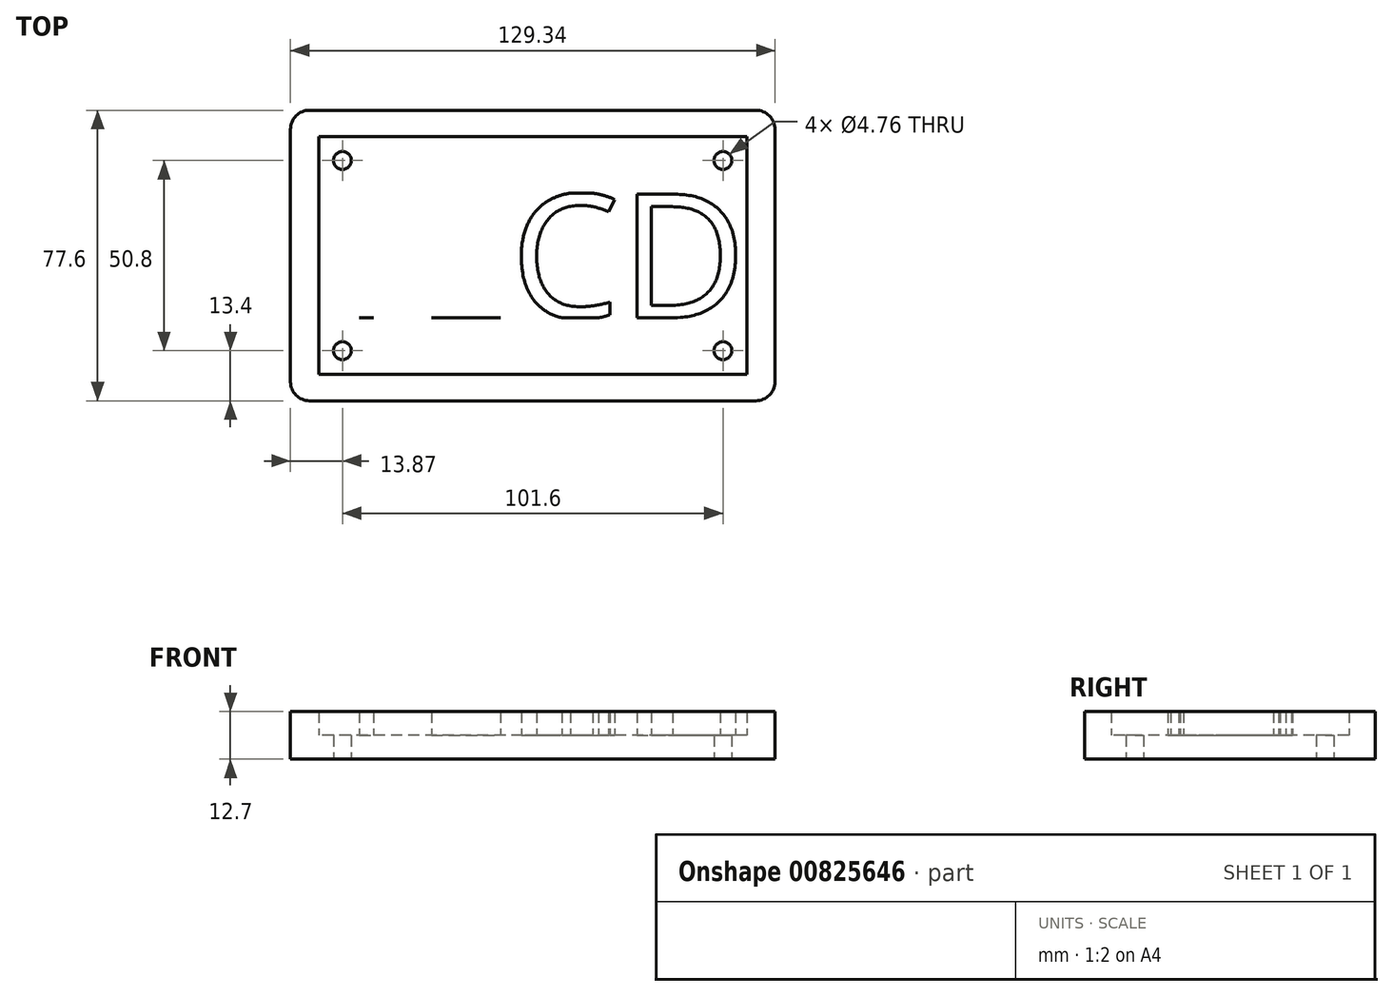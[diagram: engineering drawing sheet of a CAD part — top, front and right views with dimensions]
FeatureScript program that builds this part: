
annotation { "Feature Type Name" : "Feature", "Feature Type Description" : "" }
export const myFeature = defineFeature(function(context is Context, id is Id, definition is map)
    precondition{}
    {
        {
            var Q0;
            Q0=qCreatedBy(makeId("Top.planeOp"),FACE);
            var sketch = newSketch(context, id + "F0", { "sketchPlane" : qUnion([Q0])});
            skLineSegment(sketch, "E0.bottom", {"start": v(63.5, -38.1) * mm, "end": v(-63.5, -38.1) * mm});
            skLineSegment(sketch, "E0.top", {"start": v(63.5, 38.1) * mm, "end": v(-63.5, 38.1) * mm});
            skLineSegment(sketch, "E0.left", {"start": v(63.5, -38.1) * mm, "end": v(63.5, 38.1) * mm});
            skLineSegment(sketch, "E0.right", {"start": v(-63.5, -38.1) * mm, "end": v(-63.5, 38.1) * mm});
            skPoint(sketch, "E0.middle", {"position": v(0, 0) * mm});
            skSolve(sketch);
        }
        {
            var Q0;
            Q0=makeQuery(id+"F0.imprint","IMPRINT",FACE,{"disambiguationData":[TD([[makeQuery(id+"F0.imprint","IMPRINT",EDGE,{"derivedFrom":sQuery(id+"F0.wireOp",EDGE,"E0.bottom")}),-1.0]])]});
            extrude(context, id + "F1", {"entities" : qUnion([Q0]), "depth" : 6.35 * mm, "offsetDistance" : 25.4 * mm});
        }
        {
            var Q0;
            Q0=makeQuery(id+"F1.opExtrude","SWEPT_EDGE",EDGE,{"disambiguationData":[OSD([sQuery(id+"F0.wireOp",EDGE,"E0.top"),sQuery(id+"F0.wireOp",EDGE,"E0.right")])]});
            var Q1;
            Q1=makeQuery(id+"F1.opExtrude","SWEPT_EDGE",EDGE,{"disambiguationData":[OSD([sQuery(id+"F0.wireOp",EDGE,"E0.bottom"),sQuery(id+"F0.wireOp",EDGE,"E0.right")])]});
            var Q2;
            Q2=makeQuery(id+"F1.opExtrude","SWEPT_EDGE",EDGE,{"disambiguationData":[OSD([sQuery(id+"F0.wireOp",EDGE,"E0.bottom"),sQuery(id+"F0.wireOp",EDGE,"E0.left")])]});
            var Q3;
            Q3=makeQuery(id+"F1.opExtrude","SWEPT_EDGE",EDGE,{"disambiguationData":[OSD([sQuery(id+"F0.wireOp",EDGE,"E0.top"),sQuery(id+"F0.wireOp",EDGE,"E0.left")])]});
            fillet(context, id + "F2", {"entities" : qUnion([Q0, Q1, Q2, Q3]), "radius" : 5.08 * mm, "tangentPropagation" : true, "allowEdgeOverflow" : false});
        }
        {
            var Q0;
            Q0=makeQuery(id+"F1.opExtrude","CAP_FACE",FACE,{"disambiguationData":[OSD([sQuery(id+"F0.wireOp",EDGE,"E0.bottom"),sQuery(id+"F0.wireOp",EDGE,"E0.top"),sQuery(id+"F0.wireOp",EDGE,"E0.left"),sQuery(id+"F0.wireOp",EDGE,"E0.right")])],"isStart":false});
            cPlane(context, id + "F3", {"entities" : qUnion([Q0]), "cplaneType" : CPlaneType.OFFSET, "offset" : 0 * mm, "width" : 152.4 * mm, "height" : 152.4 * mm});
        }
        {
            var Q0;
            Q0=qCreatedBy(id+"F3.planeOp",FACE);
            var sketch = newSketch(context, id + "F4", { "sketchPlane" : qUnion([Q0])});
            skLineSegment(sketch, "E1.bottom", {"start": v(-64.67, 38.8) * mm, "end": v(64.67, 38.8) * mm});
            skLineSegment(sketch, "E1.top", {"start": v(-64.67, -38.8) * mm, "end": v(64.67, -38.8) * mm});
            skLineSegment(sketch, "E1.left", {"start": v(-64.67, 38.8) * mm, "end": v(-64.67, -38.8) * mm});
            skLineSegment(sketch, "E1.right", {"start": v(64.67, 38.8) * mm, "end": v(64.67, -38.8) * mm});
            skPoint(sketch, "E1.middle", {"position": v(0, 0) * mm});
            skLineSegment(sketch, "E2.bottom", {"start": v(-57.15, 16.64) * mm, "end": v(57.15, 16.64) * mm});
            skLineSegment(sketch, "E2.top", {"start": v(-57.15, -16.64) * mm, "end": v(57.15, -16.64) * mm});
            skLineSegment(sketch, "E2.left", {"start": v(-57.15, 16.64) * mm, "end": v(-57.15, -16.64) * mm});
            skLineSegment(sketch, "E2.right", {"start": v(57.15, 16.64) * mm, "end": v(57.15, -16.64) * mm});
            skPoint(sketch, "E3", {"position": v(-57.15, 16.64) * mm});
            skPoint(sketch, "E4", {"position": v(57.15, -16.64) * mm});
            skText(sketch, "E5", { "text": "TECD", "fontName": "OpenSans-Regular.ttf"});
            skLineSegment(sketch, "E6.bottom", {"start": v(57.15, -31.75) * mm, "end": v(-57.15, -31.75) * mm});
            skLineSegment(sketch, "E6.top", {"start": v(57.15, 31.75) * mm, "end": v(-57.15, 31.75) * mm});
            skLineSegment(sketch, "E6.left", {"start": v(57.15, -31.75) * mm, "end": v(57.15, 31.75) * mm});
            skLineSegment(sketch, "E6.right", {"start": v(-57.15, -31.75) * mm, "end": v(-57.15, 31.75) * mm});
            const initialGuessF4  = {"E5": [-0.05715, -0.01664, 1, 0, 0.03328]};
            skSetInitialGuess(sketch, initialGuessF4);
            skSolve(sketch);
        }
        {
            var Q0;
            Q0=makeQuery(id+"F4.imprint","IMPRINT",FACE,{"disambiguationData":[TD([[makeQuery(id+"F4.imprint","IMPRINT",EDGE,{"derivedFrom":sQuery(id+"F4.wireOp",EDGE,"E1.bottom")}),-1.0]])]});
            extrude(context, id + "F5", {"entities" : qUnion([Q0]), "operationType" : NewBodyOperationType.ADD, "depth" : 6.35 * mm, "offsetDistance" : 25.4 * mm});
        }
        {
            var Q0;
            Q0=makeQuery(id+"F5.opExtrude","SWEPT_EDGE",EDGE,{"disambiguationData":[OSD([sQuery(id+"F4.wireOp",EDGE,"E1.top"),sQuery(id+"F4.wireOp",EDGE,"E1.left")])]});
            var Q1;
            Q1=makeQuery(id+"F5.opExtrude","SWEPT_EDGE",EDGE,{"disambiguationData":[OSD([sQuery(id+"F4.wireOp",EDGE,"E1.bottom"),sQuery(id+"F4.wireOp",EDGE,"E1.right")])]});
            var Q2;
            Q2=makeQuery(id+"F5.opExtrude","SWEPT_EDGE",EDGE,{"disambiguationData":[OSD([sQuery(id+"F4.wireOp",EDGE,"E1.top"),sQuery(id+"F4.wireOp",EDGE,"E1.right")])]});
            var Q3;
            Q3=makeQuery(id+"F5.opExtrude","SWEPT_EDGE",EDGE,{"disambiguationData":[OSD([sQuery(id+"F4.wireOp",EDGE,"E1.bottom"),sQuery(id+"F4.wireOp",EDGE,"E1.left")])]});
            fillet(context, id + "F6", {"entities" : qUnion([Q0, Q1, Q2, Q3]), "radius" : 5.08 * mm, "tangentPropagation" : true, "allowEdgeOverflow" : false});
        }
        {
            var Q0;
            {var subQ0=sQuery(id+"F4.wireOp",EDGE,"E5.sketch_text.stroke-1");Q0=makeQuery(id+"F4.imprint","IMPRINT",FACE,{"disambiguationData":[TD([[makeQuery(id+"F4.imprint","IMPRINT",EDGE,{"derivedFrom":subQ0}),-1.0]])]});}
            var Q1;
            {var subQ0=sQuery(id+"F4.wireOp",EDGE,"E5.sketch_text.stroke-9");Q1=makeQuery(id+"F4.imprint","IMPRINT",FACE,{"disambiguationData":[TD([[makeQuery(id+"F4.imprint","IMPRINT",EDGE,{"derivedFrom":subQ0}),-1.0]])]});}
            var Q2;
            Q2=makeQuery(id+"F4.imprint","IMPRINT",FACE,{"disambiguationData":[TD([[makeQuery(id+"F4.imprint","IMPRINT",EDGE,{"derivedFrom":sQuery(id+"F4.wireOp",EDGE,"E5.sketch_text.stroke-20")}),-1.0]])]});
            var Q3;
            Q3=makeQuery(id+"F4.imprint","IMPRINT",FACE,{"disambiguationData":[TD([[makeQuery(id+"F4.imprint","IMPRINT",EDGE,{"derivedFrom":sQuery(id+"F4.wireOp",EDGE,"E5.sketch_text.stroke-35")}),-1.0]])]});
            extrude(context, id + "F7", {"entities" : qUnion([Q0, Q1, Q2, Q3]), "operationType" : NewBodyOperationType.ADD, "depth" : 6.35 * mm, "offsetDistance" : 25.4 * mm});
        }
        {
            var Q0;
            Q0=makeQuery(id+"F1.opExtrude","CAP_FACE",FACE,{"disambiguationData":[OSD([sQuery(id+"F0.wireOp",EDGE,"E0.bottom"),sQuery(id+"F0.wireOp",EDGE,"E0.top"),sQuery(id+"F0.wireOp",EDGE,"E0.left"),sQuery(id+"F0.wireOp",EDGE,"E0.right")])],"isStart":true});
            var sketch = newSketch(context, id + "F8", { "sketchPlane" : qUnion([Q0])});
            skCircle(sketch, "E7.1.1.0", {"center": v(-50.8, 25.4) * mm, "radius": 2.38 * mm});
            skCircle(sketch, "E8.1.1.0", {"center": v(50.8, 25.4) * mm, "radius": 2.38 * mm});
            skCircle(sketch, "E9.1.1.0", {"center": v(50.8, -25.4) * mm, "radius": 2.38 * mm});
            skCircle(sketch, "E10.1.1.0", {"center": v(-50.8, -25.4) * mm, "radius": 2.38 * mm});
            skSolve(sketch);
        }
        {
            var Q0;
            Q0=makeQuery(id+"F8.imprint","IMPRINT",FACE,{"disambiguationData":[TD([[makeQuery(id+"F8.imprint","IMPRINT",EDGE,{"derivedFrom":sQuery(id+"F8.wireOp",EDGE,"E7.1.1.0")}),1.0]])]});
            var Q1;
            Q1=makeQuery(id+"F8.imprint","IMPRINT",FACE,{"disambiguationData":[TD([[makeQuery(id+"F8.imprint","IMPRINT",EDGE,{"derivedFrom":sQuery(id+"F8.wireOp",EDGE,"E10.1.1.0")}),1.0]])]});
            var Q2;
            Q2=makeQuery(id+"F8.imprint","IMPRINT",FACE,{"disambiguationData":[TD([[makeQuery(id+"F8.imprint","IMPRINT",EDGE,{"derivedFrom":sQuery(id+"F8.wireOp",EDGE,"E9.1.1.0")}),1.0]])]});
            var Q3;
            Q3=makeQuery(id+"F8.imprint","IMPRINT",FACE,{"disambiguationData":[TD([[makeQuery(id+"F8.imprint","IMPRINT",EDGE,{"derivedFrom":sQuery(id+"F8.wireOp",EDGE,"E8.1.1.0")}),1.0]])]});
            extrude(context, id + "F9", {"entities" : qUnion([Q0, Q1, Q2, Q3]), "operationType" : NewBodyOperationType.REMOVE, "oppositeDirection" : true, "depth" : 25.4 * mm, "offsetDistance" : 25.4 * mm});
        }
        {
            var Q0;
            Q0=makeQuery(id+"F4.imprint","IMPRINT",FACE,{"disambiguationData":[TD([[makeQuery(id+"F4.imprint","IMPRINT",EDGE,{"derivedFrom":sQuery(id+"F4.wireOp",EDGE,"E1.bottom")}),-1.0]])]});
            extrude(context, id + "F10", {"entities" : qUnion([Q0]), "operationType" : NewBodyOperationType.ADD, "depth" : -6.35 * mm, "offsetDistance" : 25.4 * mm});
        }
        {
            var Q0;
            Q0=makeQuery(id+"F10.opExtrude","SWEPT_EDGE",EDGE,{"disambiguationData":[OSD([sQuery(id+"F4.wireOp",EDGE,"E1.bottom"),sQuery(id+"F4.wireOp",EDGE,"E1.left")])]});
            var Q1;
            Q1=makeQuery(id+"F10.opExtrude","SWEPT_EDGE",EDGE,{"disambiguationData":[OSD([sQuery(id+"F4.wireOp",EDGE,"E1.top"),sQuery(id+"F4.wireOp",EDGE,"E1.left")])]});
            var Q2;
            Q2=makeQuery(id+"F10.opExtrude","SWEPT_EDGE",EDGE,{"disambiguationData":[OSD([sQuery(id+"F4.wireOp",EDGE,"E1.top"),sQuery(id+"F4.wireOp",EDGE,"E1.right")])]});
            var Q3;
            Q3=makeQuery(id+"F10.opExtrude","SWEPT_EDGE",EDGE,{"disambiguationData":[OSD([sQuery(id+"F4.wireOp",EDGE,"E1.bottom"),sQuery(id+"F4.wireOp",EDGE,"E1.right")])]});
            fillet(context, id + "F11", {"entities" : qUnion([Q0, Q1, Q2, Q3]), "radius" : 5.08 * mm, "tangentPropagation" : true, "allowEdgeOverflow" : false});
        }
    });
